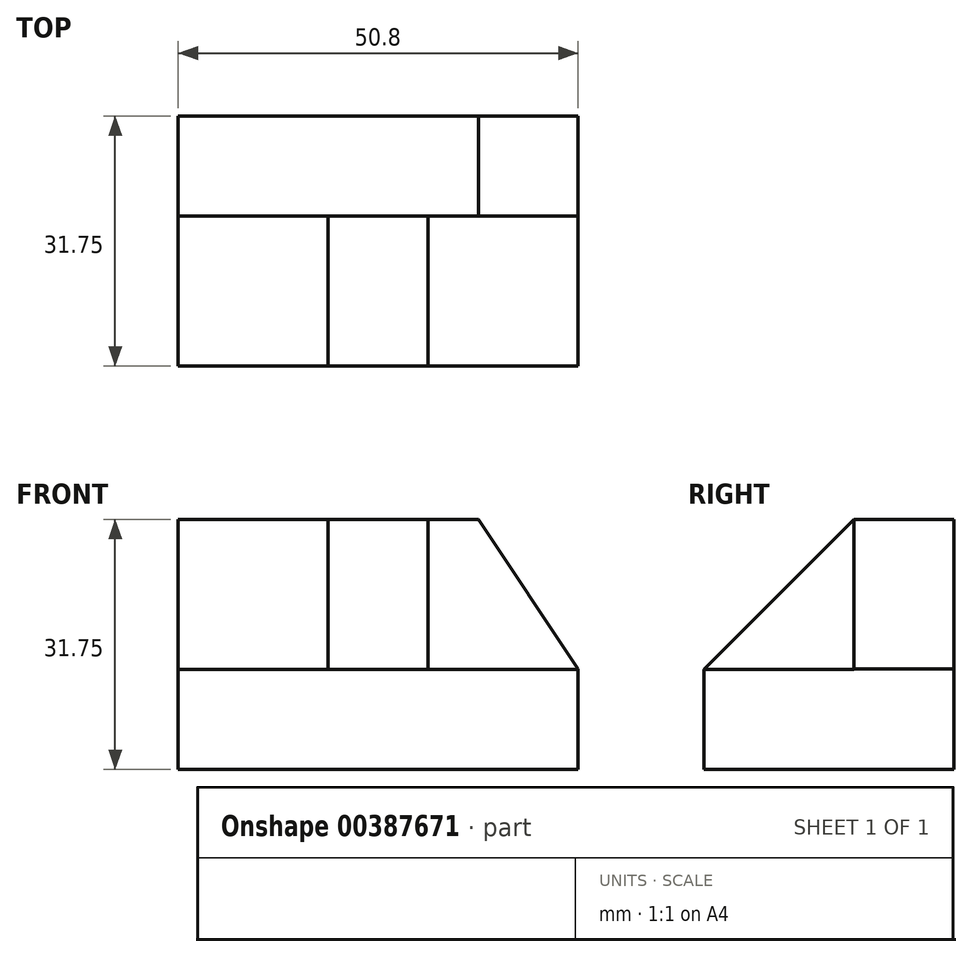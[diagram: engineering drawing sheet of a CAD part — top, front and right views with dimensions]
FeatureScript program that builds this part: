
annotation { "Feature Type Name" : "Feature", "Feature Type Description" : "" }
export const myFeature = defineFeature(function(context is Context, id is Id, definition is map)
    precondition{}
    {
        {
            var Q0;
            Q0=qCreatedBy(makeId("Right.planeOp"),FACE);
            var sketch = newSketch(context, id + "F0", { "sketchPlane" : qUnion([Q0])});
            skLineSegment(sketch, "E0", {"start": v(0, 0) * mm, "end": v(31.75, 0) * mm});
            skLineSegment(sketch, "E1", {"start": v(31.75, 0) * mm, "end": v(31.75, 31.75) * mm});
            skLineSegment(sketch, "E2", {"start": v(31.75, 31.75) * mm, "end": v(19.05, 31.75) * mm});
            skLineSegment(sketch, "E3", {"start": v(19.05, 31.75) * mm, "end": v(19.05, 12.7) * mm});
            skLineSegment(sketch, "E4", {"start": v(19.05, 12.7) * mm, "end": v(0, 12.7) * mm});
            skLineSegment(sketch, "E5", {"start": v(0, 12.7) * mm, "end": v(0, 0) * mm});
            skSolve(sketch);
        }
        {
            var Q0;
            Q0=makeQuery(id+"F0.imprint","IMPRINT",FACE,{"disambiguationData":[TD([[makeQuery(id+"F0.imprint","IMPRINT",EDGE,{"derivedFrom":sQuery(id+"F0.wireOp",EDGE,"E0")}),1.0]])]});
            extrude(context, id + "F1", {"entities" : qUnion([Q0]), "depth" : 50.8 * mm});
        }
        {
            var Q0;
            Q0=qCreatedBy(makeId("Front.planeOp"),FACE);
            var sketch = newSketch(context, id + "F2", { "sketchPlane" : qUnion([Q0])});
            skLineSegment(sketch, "E6", {"start": v(50.8, 31.81) * mm, "end": v(50.8, 12.76) * mm});
            skLineSegment(sketch, "E7", {"start": v(50.8, 12.76) * mm, "end": v(38.1, 31.81) * mm});
            skLineSegment(sketch, "E8", {"start": v(38.1, 31.81) * mm, "end": v(50.8, 31.81) * mm});
            skSolve(sketch);
        }
        {
            var Q0;
            Q0=makeQuery(id+"F2.imprint","IMPRINT",FACE,{"disambiguationData":[TD([[makeQuery(id+"F2.imprint","IMPRINT",EDGE,{"derivedFrom":sQuery(id+"F2.wireOp",EDGE,"E6")}),-1.0]])]});
            extrude(context, id + "F3", {"entities" : qUnion([Q0]), "operationType" : NewBodyOperationType.REMOVE, "oppositeDirection" : true, "depth" : 31.75 * mm});
        }
        {
            var Q0;
            Q0=qCreatedBy(makeId("Top.planeOp"),FACE);
            var sketch = newSketch(context, id + "F4", { "sketchPlane" : qUnion([Q0])});
            skLineSegment(sketch, "E9", {"start": v(19.05, 19.05) * mm, "end": v(19.05, 0) * mm});
            skLineSegment(sketch, "E10", {"start": v(19.05, 0) * mm, "end": v(31.75, 0) * mm});
            skLineSegment(sketch, "E11", {"start": v(31.75, 0) * mm, "end": v(31.75, 19.05) * mm});
            skLineSegment(sketch, "E12", {"start": v(31.75, 19.05) * mm, "end": v(19.05, 19.05) * mm});
            skSolve(sketch);
        }
        {
            var Q0;
            Q0=makeQuery(id+"F4.imprint","IMPRINT",FACE,{"disambiguationData":[TD([[makeQuery(id+"F4.imprint","IMPRINT",EDGE,{"derivedFrom":sQuery(id+"F4.wireOp",EDGE,"E9")}),1.0]])]});
            extrude(context, id + "F5", {"entities" : qUnion([Q0]), "operationType" : NewBodyOperationType.ADD, "depth" : 31.75 * mm});
        }
        {
            var Q0;
            Q0=makeQuery(id+"F5.opExtrude","SWEPT_FACE",FACE,{"disambiguationData":[OSD([sQuery(id+"F4.wireOp",EDGE,"E11")])]});
            var sketch = newSketch(context, id + "F6", { "sketchPlane" : qUnion([Q0])});
            skLineSegment(sketch, "E13", {"start": v(19.05, 31.75) * mm, "end": v(0, 12.7) * mm});
            skLineSegment(sketch, "E14", {"start": v(0, 12.7) * mm, "end": v(0, 31.75) * mm});
            skLineSegment(sketch, "E15", {"start": v(0, 31.75) * mm, "end": v(19.05, 31.75) * mm});
            skSolve(sketch);
        }
        {
            var Q0;
            Q0=makeQuery(id+"F6.imprint","IMPRINT",FACE,{"disambiguationData":[TD([[makeQuery(id+"F6.imprint","IMPRINT",EDGE,{"derivedFrom":sQuery(id+"F6.wireOp",EDGE,"E13")}),-1.0]])]});
            extrude(context, id + "F7", {"entities" : qUnion([Q0]), "operationType" : NewBodyOperationType.REMOVE, "oppositeDirection" : true, "depth" : 25.4 * mm});
        }
    });
